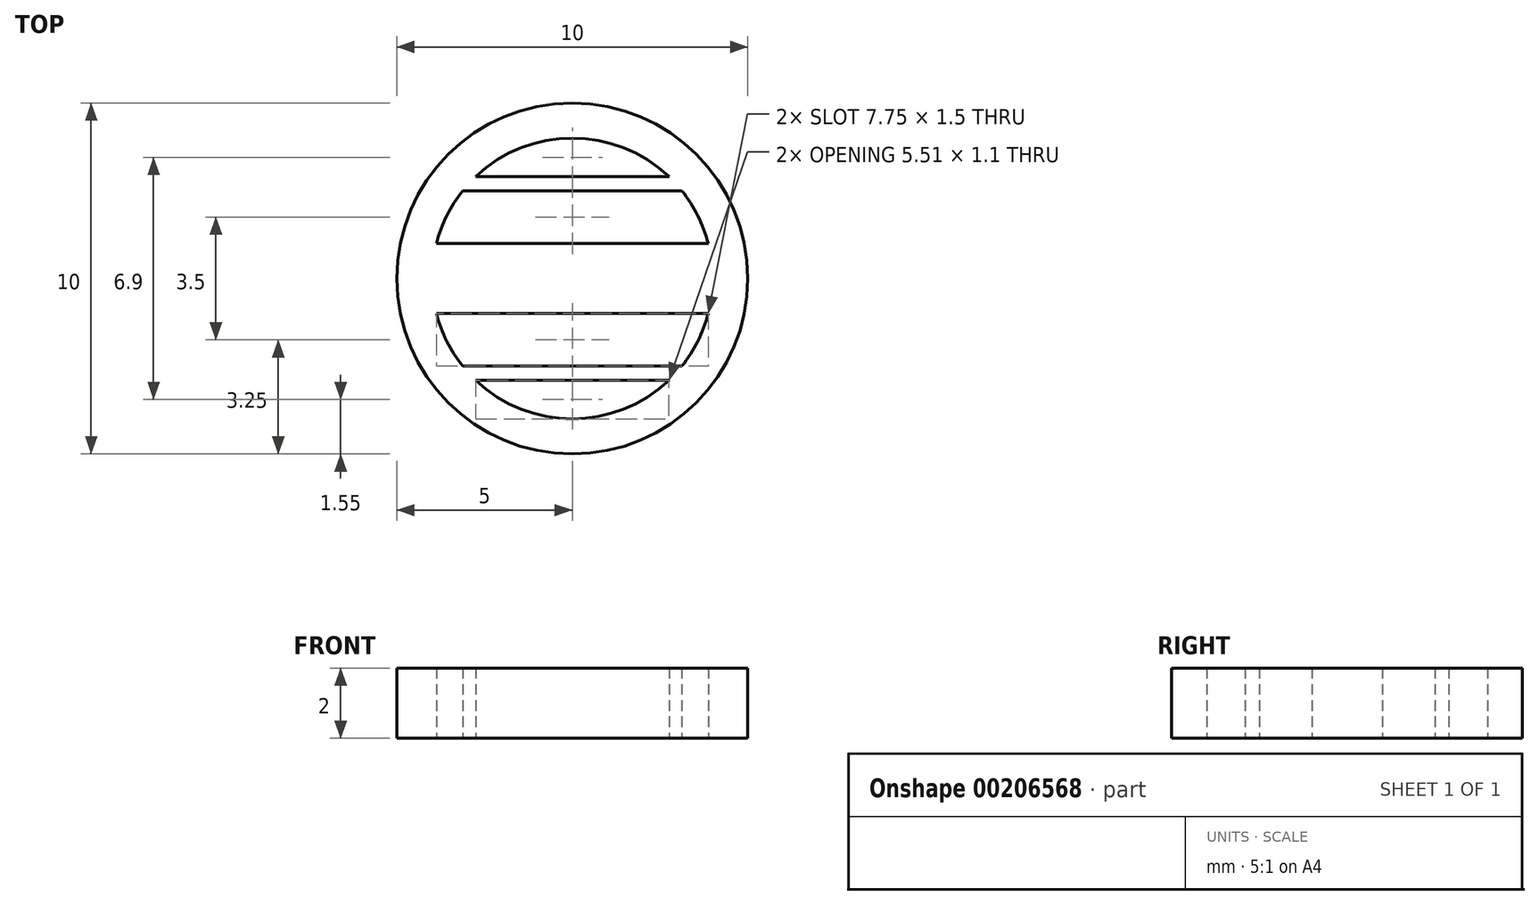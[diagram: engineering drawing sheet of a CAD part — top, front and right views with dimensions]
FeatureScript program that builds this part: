
annotation { "Feature Type Name" : "Feature", "Feature Type Description" : "" }
export const myFeature = defineFeature(function(context is Context, id is Id, definition is map)
    precondition{}
    {
        {
            var Q0;
            Q0=qCreatedBy(makeId("Top.planeOp"),FACE);
            var sketch = newSketch(context, id + "F0", { "sketchPlane" : qUnion([Q0])});
            skCircle(sketch, "E0", {"center": v(0, 0) * mm, "radius": 5 * mm});
            skCircle(sketch, "E1", {"center": v(0, 0) * mm, "radius": 4 * mm});
            skLineSegment(sketch, "E2", {"start": v(-2.1, 1) * mm, "end": v(-3.87, 1) * mm});
            skLineSegment(sketch, "E3", {"start": v(-3.87, 1) * mm, "end": v(3.87, 1) * mm});
            skLineSegment(sketch, "E4", {"start": v(-2.1, -1) * mm, "end": v(-3.87, -1) * mm});
            skLineSegment(sketch, "E5", {"start": v(-3.87, -1) * mm, "end": v(3.87, -1) * mm});
            skLineSegment(sketch, "E6", {"start": v(-2.1, -2.5) * mm, "end": v(-3.12, -2.5) * mm});
            skLineSegment(sketch, "E7", {"start": v(-3.12, -2.5) * mm, "end": v(3.12, -2.5) * mm});
            skLineSegment(sketch, "E8", {"start": v(-1.3, -2.9) * mm, "end": v(-2.75, -2.9) * mm});
            skLineSegment(sketch, "E9", {"start": v(-2.75, -2.9) * mm, "end": v(2.75, -2.9) * mm});
            skLineSegment(sketch, "E10", {"start": v(-2.1, 2.5) * mm, "end": v(-3.12, 2.5) * mm});
            skLineSegment(sketch, "E11", {"start": v(-3.12, 2.5) * mm, "end": v(3.12, 2.5) * mm});
            skLineSegment(sketch, "E12", {"start": v(-0.87, 2.9) * mm, "end": v(-2.75, 2.9) * mm});
            skLineSegment(sketch, "E13", {"start": v(-2.75, 2.9) * mm, "end": v(2.75, 2.9) * mm});
            skSolve(sketch);
        }
        {
            var Q0;
            Q0=makeQuery(id+"F0.imprint","IMPRINT",FACE,{"disambiguationData":[TD([[makeQuery(id+"F0.imprint","IMPRINT",EDGE,{"derivedFrom":sQuery(id+"F0.wireOp",EDGE,"E0")}),1.0]])]});
            extrude(context, id + "F1", {"entities" : qUnion([Q0]), "depth" : 2 * mm});
        }
        {
            var Q0;
            {var subQ0=sQuery(id+"F0.wireOp",EDGE,"E11");var subQ3=makeQuery(id+"F0.imprint","IMPRINT",VERTEX,{"derivedFrom":subQ0});Q0=makeQuery(id+"F0.imprint","IMPRINT",FACE,{"disambiguationData":[TD([[makeQuery(id+"F0.imprint","IMPRINT",EDGE,{"disambiguationData":[TD([[subQ3,1.0]])],"derivedFrom":subQ0}),1.0]])]});}
            extrude(context, id + "F2", {"entities" : qUnion([Q0]), "operationType" : NewBodyOperationType.ADD, "depth" : 2 * mm});
        }
        {
            var Q0;
            {var subQ0=sQuery(id+"F0.wireOp",EDGE,"E3");var subQ3=makeQuery(id+"F0.imprint","IMPRINT",VERTEX,{"derivedFrom":subQ0});Q0=makeQuery(id+"F0.imprint","IMPRINT",FACE,{"disambiguationData":[TD([[makeQuery(id+"F0.imprint","IMPRINT",EDGE,{"disambiguationData":[TD([[subQ3,1.0]])],"derivedFrom":subQ0}),-1.0]])]});}
            extrude(context, id + "F3", {"entities" : qUnion([Q0]), "operationType" : NewBodyOperationType.ADD, "depth" : 2 * mm});
        }
        {
            var Q0;
            {var subQ0=sQuery(id+"F0.wireOp",EDGE,"E7");var subQ3=makeQuery(id+"F0.imprint","IMPRINT",VERTEX,{"derivedFrom":subQ0});Q0=makeQuery(id+"F0.imprint","IMPRINT",FACE,{"disambiguationData":[TD([[makeQuery(id+"F0.imprint","IMPRINT",EDGE,{"disambiguationData":[TD([[subQ3,1.0]])],"derivedFrom":subQ0}),-1.0]])]});}
            extrude(context, id + "F4", {"entities" : qUnion([Q0]), "operationType" : NewBodyOperationType.ADD, "depth" : 2 * mm});
        }
    });
